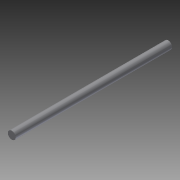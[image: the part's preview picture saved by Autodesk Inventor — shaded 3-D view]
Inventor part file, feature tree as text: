
AUTODESK INVENTOR PART (.ipt)
format: ipt  version: 2015 (Build 190159000, 159)  size: 82,432 bytes
history: native  units: in
note: dims shown in document units (in); Inventor stores cm internally (conversion verified against a paired STEP export)
features: extrude x1, other x1, imported_body x1
ambient origin geometry x8: Origin, YZ Plane, XZ Plane, XY Plane, X Axis, Y Axis, Z Axis, Center Point
bodies: Body1 (feature_tree)
feature tree (3):
  extrude  "Extrude1"  [1 undecoded]
  other  "VEX-HINGE-PIN.ipt1"
  imported_body  "Base1"
note: 1 required parameter value undecoded (feature->parameter linkage not recoverable at this tier; creation-order binding heuristic only, values carry confidence <= 0.55)
